FCSTD DOCUMENT  (FreeCAD 1.0R39109 (Git))
Label: housing_assemly
License: All rights reserved
LicenseURL: https://en.wikipedia.org/wiki/All_rights_reserved
objects: App::Link×6, Mesh::Feature×6, App::FeaturePython×4, Assembly::JointGroup×2, Assembly::AssemblyObject×2
EXTERNAL_REF file=display.FCStd obj=Body
EXTERNAL_REF file=mount_bracket.FCStd obj=Body003
EXTERNAL_REF file=display.FCStd obj=Body008
EXTERNAL_REF file=display.FCStd obj=Body009
EXTERNAL_REF file=mount_stud.FCStd obj=Body
EXTERNAL_REF file=display.FCStd obj=Spreadsheet

FEATURE [App::Link] Housing  label="Housing001"
  LinkedObject = -> <external display.FCStd>#Body
FEATURE [App::FeaturePython] GroundedJoint  # Assembly grounded joint (typed FeaturePython)
  ObjectToGround = -> Housing
FEATURE [App::Link] MountBracket
  LinkPlacement = pos=(2,0,2) rot=(0,0,1;0rad)
  LinkedObject = -> <external mount_bracket.FCStd>#Body003
  Placement = pos=(2,0,2) rot=(0,0,1;0rad)
FEATURE [App::FeaturePython] Joint  label="Fixed"  # Assembly joint (typed FeaturePython)
  Activated = true
  AngleMax = 0
  AngleMin = 0
  Detach1 = false
  Detach2 = false
  Distance = 0
  Distance2 = 0
  EnableAngleMax = false
  EnableAngleMin = false
  EnableLengthMax = false
  EnableLengthMin = false
  JointType = 0 (Fixed)
  LengthMax = 0
  LengthMin = 0
  Offset2 = pos=(0,0,0) rot=(0,0,1;3.14159rad)
  Placement1 = pos=(8.25,0,0) rot=(-0.707107,0,0.707107;3.14159rad)
  Placement2 = pos=(6.25,0,0) rot=(0,-1,0;4.71239rad)
  Reference1 = -> Assembly [Housing.Sketch033.Edge4,Housing.Sketch033.Edge4]
  Reference2 = -> Assembly [MountBracket.Edge2,MountBracket.Edge2]
FEATURE [Assembly::JointGroup] Joints
  Group = -> [GroundedJoint,Joint]
FEATURE [Mesh::Feature] Mesh  label="Housing (Meshed)"
FEATURE [App::Link] LeftBackPlateBody001
  LinkPlacement = pos=(87,-1.03712e-05,0) rot=(0,0,1;0rad)
  LinkedObject = -> <external display.FCStd>#Body008
  Placement = pos=(87,-1.03712e-05,0) rot=(0,0,1;0rad)
FEATURE [Mesh::Feature] Mesh001  label="LeftBackPlateBody (Meshed)"
FEATURE [App::Link] RightBackPlateBody
  LinkedObject = -> <external display.FCStd>#Body009
FEATURE [Mesh::Feature] Mesh002  label="RightBackPlateBody (Meshed)"
FEATURE [Mesh::Feature] Mesh003  label="BackPlate (Meshed)"
FEATURE [Mesh::Feature] Mesh004  label="BackPlate (Meshed)001"
FEATURE [App::Link] MountStud
  LinkPlacement = pos=(112.188,-13.3202,62.1352) rot=(0,0,1;0rad)
  LinkedObject = -> <external mount_stud.FCStd>#Body
  Placement = pos=(112.188,-13.3202,62.1352) rot=(0,0,1;0rad)
FEATURE [App::Link] MountStud001
  LinkPlacement = pos=(80.8,-4,23.3932) rot=(0.57735,-0.57735,0.57735;2.0944rad)
  LinkedObject = -> <external mount_stud.FCStd>#Body
  Placement = pos=(80.8,-4,23.3932) rot=(0.57735,-0.57735,0.57735;2.0944rad)
FEATURE [App::FeaturePython] GroundedJoint001  # Assembly grounded joint (typed FeaturePython)
  ObjectToGround = -> RightBackPlateBody
FEATURE [App::FeaturePython] Joint001  label="Fixed001"  # Assembly joint (typed FeaturePython)
  Activated = true
  AngleMax = 0
  AngleMin = 0
  Detach1 = false
  Detach2 = false
  Distance = 0
  Distance2 = 0
  EnableAngleMax = false
  EnableAngleMin = false
  EnableLengthMax = false
  EnableLengthMin = false
  JointType = 0 (Fixed)
  LengthMax = 0
  LengthMin = 0
  Offset1 = pos=(0,4,0) rot=(0,0,1;0rad)
  Offset2 = pos=(0,0,0) rot=(0,0,1;1.5708rad)
  Placement1 = pos=(4.63675,-4,0) rot=(0.707107,0,0.707107;3.14159rad)
  Placement2 = pos=(80.8,28.0299,0) rot=(-1,0,0;1.5708rad)
  Reference1 = -> Assembly [Assembly001.MountStud001.Sketch.Edge4,Assembly001.MountStud001.Sketch.Edge4]
  Reference2 = -> Assembly [Assembly001.RightBackPlateBody.Sketch042.Edge2,Assembly001.RightBackPlateBody.Sketch042.Edge2]
  expr: .Offset1.Base.y = display#<<DisplaySS>>.back_plate_thickness
FEATURE [Assembly::JointGroup] Joints001
  Group = -> [GroundedJoint001,Joint001]
FEATURE [Assembly::AssemblyObject] Assembly001  label="BackPlate"
  Group = -> [Joints001,LeftBackPlateBody001,RightBackPlateBody,MountStud,MountStud001,GroundedJoint001,Joint001]
  Origin = -> Origin001
  Type = Assembly
FEATURE [Assembly::AssemblyObject] Assembly  label="Housing"
  Group = -> [Joints,Housing,GroundedJoint,MountBracket,Joint,Assembly001]
  Origin = -> Origin
  Type = Assembly
FEATURE [Mesh::Feature] Mesh005  label="BackPlate (Meshed)002"

RESOLVED EXTERNAL PARTS (link-assembly join: the EXTERNAL_REF files above that resolve inside this repo's crawl, each included once):
---- part display.FCStd = doc fcstd_653ebc197c7e (121614 chars; too large to inline — full recipe in that document) ----
---- part mount_bracket.FCStd = doc fcstd_4642901b0343 ----
FCSTD DOCUMENT  (FreeCAD 1.0R39109 (Git))
Label: mount_bracket
License: All rights reserved
LicenseURL: https://en.wikipedia.org/wiki/All_rights_reserved
objects: Sketcher::SketchObject×3, PartDesign::Pocket×2, Spreadsheet::Sheet×1, PartDesign::Plane×1, PartDesign::Pad×1, PartDesign::Body×1
note: 17 computed .brp shape members not serialized (recipe doc carries the construction recipe); baked Part::Feature solids carry a one-line shape summary decoded from their .brp

FEATURE [Spreadsheet::Sheet] Spreadsheet  label="DisplaySS"
  Configuration = 1
  cells = A1='Variant; B1='threaded_insert_depth; C1='squared_profile_section_length; D1='threaded_insert_outer_diameter; E1='threaded_insert_safety_zone; F1='mount_bracket_face_size; G1='mount_bracket_length; H1='mount_bracket_draft_angle; I1='rear_countersink_offset; J1='rear_countersink_diameter; K1='rear_countersink_depth; A2==hiddenref(.Configuration.String); B2(threaded_insert_depth)==.B4; C2(squared_profile_section_length)==.C4; D2(threaded_insert_outer_diameter)==.D4; E2(threaded_insert_safety_zone)==.E4; F2(mount_bracket_face_size)==.F4; G2(mount_bracket_length)==.G4; H2(mount_bracket_draft_angle)==.H4; I2(rear_countersink_offset)==.I4; J2(rear_countersink_diameter)==.J4; K2(rear_countersink_depth)==.K4; A3='Female; B3==4 mm; C3==threaded_insert_depth; D3==5 mm; E3==2 mm; F3==12.5 mm; G3==mount_bracket_face_size / tan(mount_bracket_draft_angle) + threaded_insert_depth; H3==35 deg; I3==0 mm; J3==threaded_insert_outer_diameter; K3==threaded_insert_depth; A4='Male; B4==50 mm; C4==4 mm; D4==2 mm; E4==1 mm; F4==12.5 mm; G4==mount_bracket_face_size / tan(mount_bracket_draft_angle) + squared_profile_section_length; H4==35 deg; I4==squared_profile_section_length; J4==4 mm; K4==mount_bracket_length
  expr: .Configuration.Enum = cells[<<A3:|>>]
  expr: .cells.Bind.B2.ZZ2 = tuple(.cells; <<B>> + str(hiddenref(Configuration) + 3); <<ZZ>> + str(hiddenref(Configuration) + 3))
FEATURE [Sketcher::SketchObject] Sketch011  label="Threaded Barrel"
  ArcFitTolerance = 1e-06
  AttachmentSupport = -> [XZ_Plane003]
  FullyConstrained = true
  MakeInternals = false
  MapMode = 5
  Placement = pos=(0,0,0) rot=(1,0,0;1.5708rad)
  expr: Constraints[0] = <<DisplaySS>>.threaded_insert_outer_diameter
  expr: Constraints[1] = <<DisplaySS>>.mount_bracket_face_size / 2
  expr: Constraints[2] = <<DisplaySS>>.mount_bracket_face_size / 2
  sketch-geometry (1):
    g0: Circle CenterX=6.25 CenterY=6.25 CenterZ=0 NormalX=0 NormalY=0 NormalZ=1 AngleXU=0 Radius=1
  constraints (3):
    c: Diameter(g0) = 2
    c: DistanceY(g-1,g0) = 6.25
    c: DistanceX(g-2,g0) = 6.25
FEATURE [Sketcher::SketchObject] Sketch010
  ArcFitTolerance = 1e-06
  AttachmentSupport = -> [XY_Plane003]
  FullyConstrained = true
  MakeInternals = false
  MapMode = 4
  Placement = pos=(0,0,0) rot=(0.57735,0.57735,0.57735;2.0944rad)
  expr: Constraints[10] = <<DisplaySS>>.mount_bracket_face_size
  expr: Constraints[8] = <<DisplaySS>>.mount_bracket_draft_angle
  expr: Constraints[9] = <<DisplaySS>>.squared_profile_section_length
  sketch-geometry (4):
    g0: LineSegment StartX=-21.8519 StartY=-1.8e-15 StartZ=0 EndX=0 EndY=0 EndZ=0
    g1: LineSegment StartX=0 StartY=0 StartZ=0 EndX=0 EndY=12.5 EndZ=0
    g2: LineSegment StartX=0 StartY=12.5 StartZ=0 EndX=-4 EndY=12.5 EndZ=0
    g3: LineSegment StartX=-4 StartY=12.5 StartZ=0 EndX=-21.8519 EndY=-1.8e-15 EndZ=0
  constraints (11):
    c: PointOnObject(g0,g-1)
    c: Coincident(g0,g-1)
    c: Coincident(g0,g1)
    c: PointOnObject(g1,g-2)
    c: Coincident(g1,g2)
    c: Horizontal(g2)
    c: Coincident(g2,g3)
    c: Coincident(g3,g0)
    c: Angle(g0,g3) = 0.610865
    c: Distance(g2) = 4
    c: Distance(g1) = 12.5
FEATURE [PartDesign::Plane] DatumPlane  label="CountersinkPlane"
  AttachmentOffset = pos=(0,0,4) rot=(0,0,1;0rad)
  AttachmentSupport = -> [XZ_Plane003]
  Length = 60
  MapMode = 5
  Placement = pos=(0,-4,9e-16) rot=(1,0,0;1.5708rad)
  ResizeMode = 0
  Width = 60
  expr: .AttachmentOffset.Base.z = <<DisplaySS>>.rear_countersink_offset
FEATURE [Sketcher::SketchObject] Sketch  label="CountersinkSketch"
  ArcFitTolerance = 1e-06
  AttachmentSupport = -> [DatumPlane]
  ExternalGeometry = -> [Sketch011]
  FullyConstrained = true
  MakeInternals = false
  MapMode = 5
  Placement = pos=(0,-4,9e-16) rot=(1,0,0;1.5708rad)
  expr: Constraints[1] = <<DisplaySS>>.rear_countersink_diameter
  sketch-geometry (1):
    g0: Circle CenterX=6.25 CenterY=6.25 CenterZ=0 NormalX=0 NormalY=0 NormalZ=1 AngleXU=0 Radius=2
  constraints (2):
    c: Coincident(g0,g-3)
    c: Diameter(g0) = 4
FEATURE [PartDesign::Pad] Pad006
  Direction = (1,0,0)
  Length = 12.5
  Length2 = 10
  Profile = -> Sketch010
  ReferenceAxis = -> Sketch010 [N_Axis]
  Refine = true
  Suppressed = false
  Type = 0
  expr: Length = <<DisplaySS>>.mount_bracket_face_size
FEATURE [PartDesign::Pocket] Pocket015
  BaseFeature = -> Pad006
  Direction = (0,1,-2e-16)
  Length = 50
  Length2 = 5
  Profile = -> Sketch011
  ReferenceAxis = -> Sketch011 [N_Axis]
  Refine = true
  Reversed = true
  Suppressed = false
  Type = 0
  expr: Length = <<DisplaySS>>.threaded_insert_depth
FEATURE [PartDesign::Pocket] Pocket
  BaseFeature = -> Pocket015
  Direction = (0,1,-2e-16)
  Length = 21.8519
  Length2 = 5
  Profile = -> Sketch
  ReferenceAxis = -> Sketch [N_Axis]
  Refine = true
  Reversed = true
  Suppressed = false
  Type = 0
  expr: Length = <<DisplaySS>>.rear_countersink_depth
FEATURE [PartDesign::Body] Body003  label="MountBracket"
  AllowCompound = false
  Group = -> [Sketch010,Pad006,Sketch011,Pocket015,Sketch,Pocket,DatumPlane]
  Origin = -> Origin003
  Tip = -> Pocket
---- part mount_stud.FCStd = doc fcstd_6881cdc6e3de ----
FCSTD DOCUMENT  (FreeCAD 1.0R39109 (Git))
Label: mount_stud
License: All rights reserved
LicenseURL: https://en.wikipedia.org/wiki/All_rights_reserved
objects: Spreadsheet::Sheet×1, Sketcher::SketchObject×1, PartDesign::Revolution×1, PartDesign::Body×1
note: 6 computed .brp shape members not serialized (recipe doc carries the construction recipe); baked Part::Feature solids carry a one-line shape summary decoded from their .brp

FEATURE [Spreadsheet::Sheet] Spreadsheet002  label="MountStudSS"
  Body = 0
  cells = B1='height; C1='base_diameter; D1='top_diameter; E1='barrel_diameter; F1='barrel_depth; G1='depth_padding; H1='horizontal_padding; I1='slope_angle; J1='top_diameter_excluding_barrel; A2==hiddenref(.Body.String); B2(height)==.B3; C2(base_diameter)==.C3; D2(top_diameter)==.D3; E2(barrel_diameter)==.E3; F2(barrel_depth)==.F3; G2(depth_padding)==.G3; H2(horizontal_padding)==.H3; I2(slope_angle)==.I3; J2(top_diameter_excluding_barrel)==.J3; A3='M2 Heated; B3==10 mm; C3==tan(slope_angle) * height * 2 + top_diameter; D3==barrel_diameter + horizontal_padding; E3==5 mm; F3==4 mm; G3==2 mm; H3==2 mm; I3==30 deg; J3==top_diameter - barrel_diameter
  expr: .Body.Enum = cells[<<A3:|>>]
  expr: .cells.Bind.B2.ZZ2 = tuple(.cells; <<B>> + str(hiddenref(Body) + 3); <<ZZ>> + str(hiddenref(Body) + 3))
FEATURE [Sketcher::SketchObject] Sketch
  ArcFitTolerance = 1e-06
  AttachmentSupport = -> [XZ_Plane]
  FullyConstrained = true
  MakeInternals = false
  MapMode = 5
  Placement = pos=(0,0,0) rot=(1,0,0;1.5708rad)
  expr: Constraints[10] = <<MountStudSS>>.barrel_diameter / 2
  expr: Constraints[13] = <<MountStudSS>>.barrel_depth
  expr: Constraints[14] = <<MountStudSS>>.top_diameter_excluding_barrel
  expr: Constraints[15] = <<MountStudSS>>.height
  expr: Constraints[16] = <<MountStudSS>>.base_diameter / 2
  sketch-geometry (6):
    g0: LineSegment StartX=2.5 StartY=10 StartZ=0 EndX=2.5 EndY=6 EndZ=0
    g1: LineSegment StartX=2.5 StartY=6 StartZ=0 EndX=0 EndY=6 EndZ=0
    g2: LineSegment StartX=0 StartY=6 StartZ=0 EndX=0 EndY=0 EndZ=0
    g3: LineSegment StartX=0 StartY=0 StartZ=0 EndX=9.2735 EndY=0 EndZ=0
    g4: LineSegment StartX=9.2735 StartY=0 StartZ=0 EndX=4.5 EndY=10 EndZ=0
    g5: LineSegment StartX=4.5 StartY=10 StartZ=0 EndX=2.5 EndY=10 EndZ=0
  constraints (17):
    c: Vertical(g0)
    c: Coincident(g0,g1)
    c: Coincident(g1,g2)
    c: Coincident(g2,g-1)
    c: Vertical(g2)
    c: Coincident(g2,g3)
    c: PointOnObject(g3,g-1)
    c: Coincident(g3,g4)
    c: Coincident(g4,g5)
    c: Coincident(g5,g0)
    c: Distance(g1) = 2.5
    c: Angle(g0,g1) = 1.5708
    c: Angle(g0,g5) = 1.5708
    c: Distance(g0) = 4
    c: Distance(g5) = 2
    c: DistanceY(g-1,g0) = 10
    c: Distance(g3) = 9.2735
FEATURE [PartDesign::Revolution] Revolution
  Angle = 360
  Angle2 = 60
  Axis = (0,2e-16,1)
  Base = (0,0,0)
  Placement = pos=(0,0,0) rot=(1,0,0;1.5708rad)
  Profile = -> Sketch
  ReferenceAxis = -> Sketch [V_Axis]
  Refine = true
  Reversed = true
  Suppressed = false
  Type = 0
FEATURE [PartDesign::Body] Body  label="MountStud"
  AllowCompound = false
  Group = -> [Sketch,Revolution]
  Origin = -> Origin
  Tip = -> Revolution
